# Revit family: svetilnik_alfresco_solyaris-5
name_source: partatom
category: Осветительные приборы
revit_build: Autodesk Revit 2016 (Build: 20150714_1515(x64)
units: mm (PartAtom-declared; Revit-internal decimal feet)

## family parameters
Всегда вертикально = Да
Источник света = Да
На основе рабочей плоскости = Нет
Общий = Нет
При загрузке вырезать с полостями = Нет
Размер круглого соединителя = Использовать диаметр
Тип детали = Нормальный
Точка расчета площади = Нет

## types (2) — shared parameters
ADSK_Артикул = СЛС52
ADSK_Единица измерения = шт
ADSK_Классификация нагрузок = Освещение
ADSK_Количество фаз = 2
ADSK_Количество фаз числовое = 2
ADSK_Коэффициент мощности = 0.97
ADSK_Масса = 111
ADSK_Модель = Солярис 5
ADSK_Напряжение = 220 В
ADSK_Размер_Высота = 4200 мм
ADSK_Размер_Длина = 1000 мм
ADSK_Размер_Ширина = 1000 мм
ADSK_Ток = 0 А
ADSK_Энергоэффективность = 90 лм/Вт
IP Class = IP 54
URL = http://www.allfresco.ru
Блок аварийного питания = Нет
Видимая форма излучения при визуализации = Нет
Изготовитель = ALFRESCO
Излучение по диаметру окружности = 120 мм
Класс Защиты = 1
Класс пожароопасности = F (светильники предназначены для установки непосредственно на поверхность из нормально воспламеняемых матеоиалов)
Климатическая зона = У1
Область использования = Ландшафт, коттедж.поселки,микрорайоны,АЗС, автостоянки
Светофильтр = 16777215
Смещение цветовой температуры при затухании лампы = <Нет>
Температура эксплуатации = -35 +40
Тип ИС = МГЛ-лампа
Тип КСС = Sym
Тип ПРА = ЭМПРА
Тип продукции = Уличный светильник
Угол наклона = 90.00°
Файл фотометрической сетки = прожектор для Солярис 5 LED 10W.ies
Цветовая температура = 4000

## per-type parameters (varying)
| type | ADSK_Наименование | ADSK_Номинальная мощность | ADSK_Полная мощность | Полная установленная мощность | Световой поток | Тип светильника |
| Солярис-5-LED9-150Вт | Светильник уличный Солярис-5-LED9 (150Вт) | 150 Вт | 155 В·А | 155 В·А | 13500 лм | Солярис5 : 150Вт |
| Солярис-5-LED9-70Вт | Светильник уличный Солярис-5-LED9 (70Вт) | 70 Вт | 72 В·А | 72 В·А | 6300 лм | Солярис5 : 70Вт |
